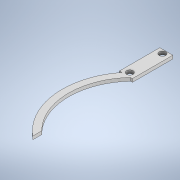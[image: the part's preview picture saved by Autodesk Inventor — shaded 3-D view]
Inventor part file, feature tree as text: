
AUTODESK INVENTOR PART (.ipt)
format: ipt  version: 2021 (Build 250183000, 183)  size: 124,416 bytes
history: native  units: in
note: dims shown in document units (in); Inventor stores cm internally (conversion verified against a paired STEP export)
features: sketch x2, extrude x1, hole x1, projected_geometry x1
ambient origin geometry x8: Origin, YZ Plane, XZ Plane, XY Plane, X Axis, Y Axis, Z Axis, Center Point
bodies: Solid1 (feature_tree)
feature tree (5):
  extrude  "Extrusion1"  Depth=0.5in
  hole  "Hole1"  [1 undecoded]
  sketch  "Sketch1"  dims[d0=2.5in d2=0.5in]
  sketch  "Sketch2"  dims[d3=1.55in d4=0.125in d5=0.0in d6=0.5in d7=0.25in d8=0.25in d9=1.25in d10=1.55in d11=0.15in d12=0.25in d13=0.75in d14=0.375in d15=0.25in d16=0.5635in d17=0.75in d18=0.8108in]
  projected_geometry  "Projected Loop1"
note: 1 required parameter value undecoded (feature->parameter linkage not recoverable at this tier; creation-order binding heuristic only, values carry confidence <= 0.55)
